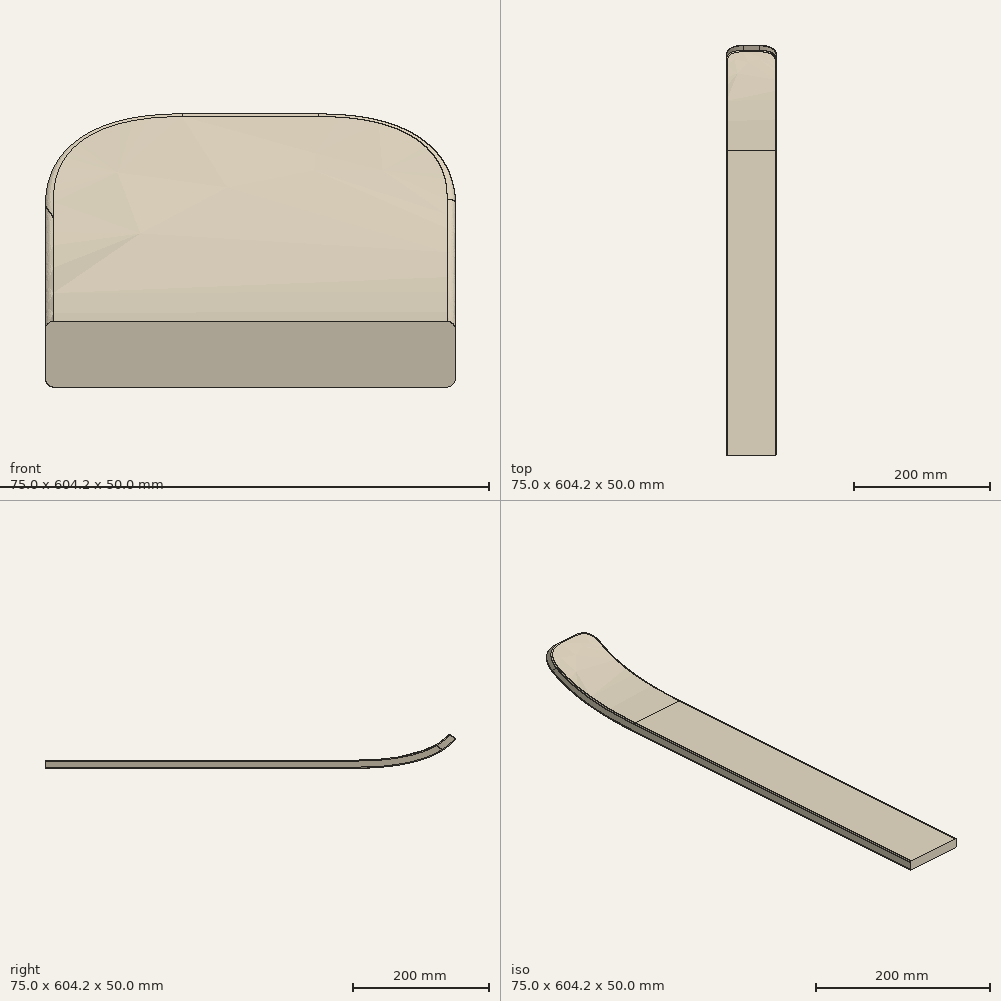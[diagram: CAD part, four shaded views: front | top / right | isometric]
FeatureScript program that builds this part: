
annotation { "Feature Type Name" : "Feature", "Feature Type Description" : "" }
export const myFeature = defineFeature(function(context is Context, id is Id, definition is map)
    precondition{}
    {
        {
            var Q0;
            Q0=qCreatedBy(makeId("Front.planeOp"),FACE);
            var sketch = newSketch(context, id + "F0", { "sketchPlane" : qUnion([Q0])});
            skLineSegment(sketch, "E0.bottom", {"start": v(36, 6) * mm, "end": v(-36, 6) * mm});
            skLineSegment(sketch, "E0.top", {"start": v(36, -6) * mm, "end": v(-36, -6) * mm});
            skLineSegment(sketch, "E0.left", {"start": v(37.5, 4.5) * mm, "end": v(37.5, -4.5) * mm});
            skLineSegment(sketch, "E0.right", {"start": v(-37.5, 4.5) * mm, "end": v(-37.5, -4.5) * mm});
            skPoint(sketch, "E0.middle", {"position": v(0, 0) * mm});
            skPoint(sketch, "E1.visualSharp", {"position": v(-37.5, 6) * mm});
            skArc(sketch, "E1.filletArc", {"start": v(-36, 6) * mm, "mid": v(-37.06, 5.56) * mm, "end": v(-37.5, 4.5) * mm});
            skPoint(sketch, "E2.visualSharp", {"position": v(37.5, 6) * mm});
            skArc(sketch, "E2.filletArc", {"start": v(37.5, 4.5) * mm, "mid": v(37.06, 5.56) * mm, "end": v(36, 6) * mm});
            skPoint(sketch, "E3.visualSharp", {"position": v(37.5, -6) * mm});
            skArc(sketch, "E3.filletArc", {"start": v(36, -6) * mm, "mid": v(37.06, -5.56) * mm, "end": v(37.5, -4.5) * mm});
            skPoint(sketch, "E4.visualSharp", {"position": v(-37.5, -6) * mm});
            skArc(sketch, "E4.filletArc", {"start": v(-37.5, -4.5) * mm, "mid": v(-37.06, -5.56) * mm, "end": v(-36, -6) * mm});
            skSolve(sketch);
        }
        {
            var Q0;
            Q0=qCreatedBy(makeId("Right.planeOp"),FACE);
            var sketch = newSketch(context, id + "F1", { "sketchPlane" : qUnion([Q0])});
            skLineSegment(sketch, "E5", {"start": v(0, 6) * mm, "end": v(450, 6) * mm});
            skFitSpline(sketch, "E6", {"points": [v(450, 6) * mm, v(595.74, 44.6) * mm], "startDerivative": vector(162.65, 0) * mm, "endDerivative": vector(84.34, 97.17) * mm});
            skSolve(sketch);
        }
        {
            var Q0;
            Q0=makeQuery(id+"F0.imprint","IMPRINT",FACE,{"disambiguationData":[TD([[makeQuery(id+"F0.imprint","IMPRINT",EDGE,{"derivedFrom":sQuery(id+"F0.wireOp",EDGE,"E0.bottom")}),1.0]])]});
            var Q1;
            Q1=sQuery(id+"F1.wireOp",EDGE,"E5");
            var Q2;
            Q2=sQuery(id+"F1.wireOp",EDGE,"E6");
            sweep(context, id + "F2", {"profiles" : qUnion([Q0]), "path" : qUnion([Q1, Q2])});
        }
        {
            var Q0;
            Q0=makeQuery(id+"F2.opSweep","CAP_EDGE",EDGE,{"disambiguationData":[OSD([sQuery(id+"F0.wireOp",EDGE,"E0.bottom"),sQuery(id+"F1.wireOp",VERTEX,"E6.end")])],"isStart":false});
            var Q1;
            Q1=makeQuery(id+"F2.opSweep","CAP_EDGE",EDGE,{"disambiguationData":[OSD([sQuery(id+"F0.wireOp",EDGE,"E0.top"),sQuery(id+"F1.wireOp",VERTEX,"E6.end")])],"isStart":false});
            fillet(context, id + "F3", {"entities" : qUnion([Q0, Q1]), "radius" : 1.5 * mm, "allowEdgeOverflow" : false});
        }
        {
            var Q0;
            Q0=makeQuery(id+"F2.opSweep","CAP_EDGE",EDGE,{"disambiguationData":[OSD([sQuery(id+"F0.wireOp",EDGE,"E0.right"),sQuery(id+"F1.wireOp",VERTEX,"E6.end")])],"isStart":false});
            var Q1;
            Q1=makeQuery(id+"F2.opSweep","CAP_EDGE",EDGE,{"disambiguationData":[OSD([sQuery(id+"F0.wireOp",EDGE,"E0.left"),sQuery(id+"F1.wireOp",VERTEX,"E6.end")])],"isStart":false});
            fillet(context, id + "F4", {"entities" : qUnion([Q0, Q1]), "radius" : 25 * mm, "rho" : 0.5, "crossSection" : FilletCrossSection.CONIC, "allowEdgeOverflow" : false});
        }
        {
            var Q0;
            Q0=makeQuery(id+"F4.opFillet","BLEND_EDGE",EDGE,{"blendedFrom":[makeQuery(id+"F2.opSweep","CAP_EDGE",EDGE,{"disambiguationData":[OSD([sQuery(id+"F0.wireOp",EDGE,"E0.left"),sQuery(id+"F1.wireOp",VERTEX,"E6.end")])],"isStart":false}),makeQuery(id+"F2.opSweep","SWEPT_FACE",FACE,{"disambiguationData":[OSD([sQuery(id+"F0.wireOp",EDGE,"E0.bottom"),sQuery(id+"F1.wireOp",EDGE,"E6")])]})],"blendedInto":[makeQuery(id+"F2.opSweep","SWEPT_FACE",FACE,{"disambiguationData":[OSD([sQuery(id+"F0.wireOp",EDGE,"E0.bottom"),sQuery(id+"F1.wireOp",EDGE,"E6")])]})]});
            var Q1;
            Q1=makeQuery(id+"F4.opFillet","BLEND_EDGE",EDGE,{"blendedFrom":[makeQuery(id+"F2.opSweep","CAP_EDGE",EDGE,{"disambiguationData":[OSD([sQuery(id+"F0.wireOp",EDGE,"E0.right"),sQuery(id+"F1.wireOp",VERTEX,"E6.end")])],"isStart":false}),makeQuery(id+"F2.opSweep","SWEPT_FACE",FACE,{"disambiguationData":[OSD([sQuery(id+"F0.wireOp",EDGE,"E0.bottom"),sQuery(id+"F1.wireOp",EDGE,"E6")])]})],"blendedInto":[makeQuery(id+"F2.opSweep","SWEPT_FACE",FACE,{"disambiguationData":[OSD([sQuery(id+"F0.wireOp",EDGE,"E0.bottom"),sQuery(id+"F1.wireOp",EDGE,"E6")])]})]});
            var Q2;
            Q2=makeQuery(id+"F4.opFillet","BLEND_EDGE",EDGE,{"blendedFrom":[makeQuery(id+"F2.opSweep","CAP_EDGE",EDGE,{"disambiguationData":[OSD([sQuery(id+"F0.wireOp",EDGE,"E0.left"),sQuery(id+"F1.wireOp",VERTEX,"E6.end")])],"isStart":false}),makeQuery(id+"F2.opSweep","SWEPT_FACE",FACE,{"disambiguationData":[OSD([sQuery(id+"F0.wireOp",EDGE,"E0.top"),sQuery(id+"F1.wireOp",EDGE,"E6")])]})],"blendedInto":[makeQuery(id+"F2.opSweep","SWEPT_FACE",FACE,{"disambiguationData":[OSD([sQuery(id+"F0.wireOp",EDGE,"E0.top"),sQuery(id+"F1.wireOp",EDGE,"E6")])]})]});
            var Q3;
            Q3=makeQuery(id+"F4.opFillet","BLEND_EDGE",EDGE,{"blendedFrom":[makeQuery(id+"F2.opSweep","CAP_EDGE",EDGE,{"disambiguationData":[OSD([sQuery(id+"F0.wireOp",EDGE,"E0.right"),sQuery(id+"F1.wireOp",VERTEX,"E6.end")])],"isStart":false}),makeQuery(id+"F2.opSweep","SWEPT_FACE",FACE,{"disambiguationData":[OSD([sQuery(id+"F0.wireOp",EDGE,"E0.top"),sQuery(id+"F1.wireOp",EDGE,"E6")])]})],"blendedInto":[makeQuery(id+"F2.opSweep","SWEPT_FACE",FACE,{"disambiguationData":[OSD([sQuery(id+"F0.wireOp",EDGE,"E0.top"),sQuery(id+"F1.wireOp",EDGE,"E6")])]})]});
            fillet(context, id + "F5", {"entities" : qUnion([Q0, Q1, Q2, Q3]), "radius" : 1.5 * mm, "allowEdgeOverflow" : false});
        }
    });
